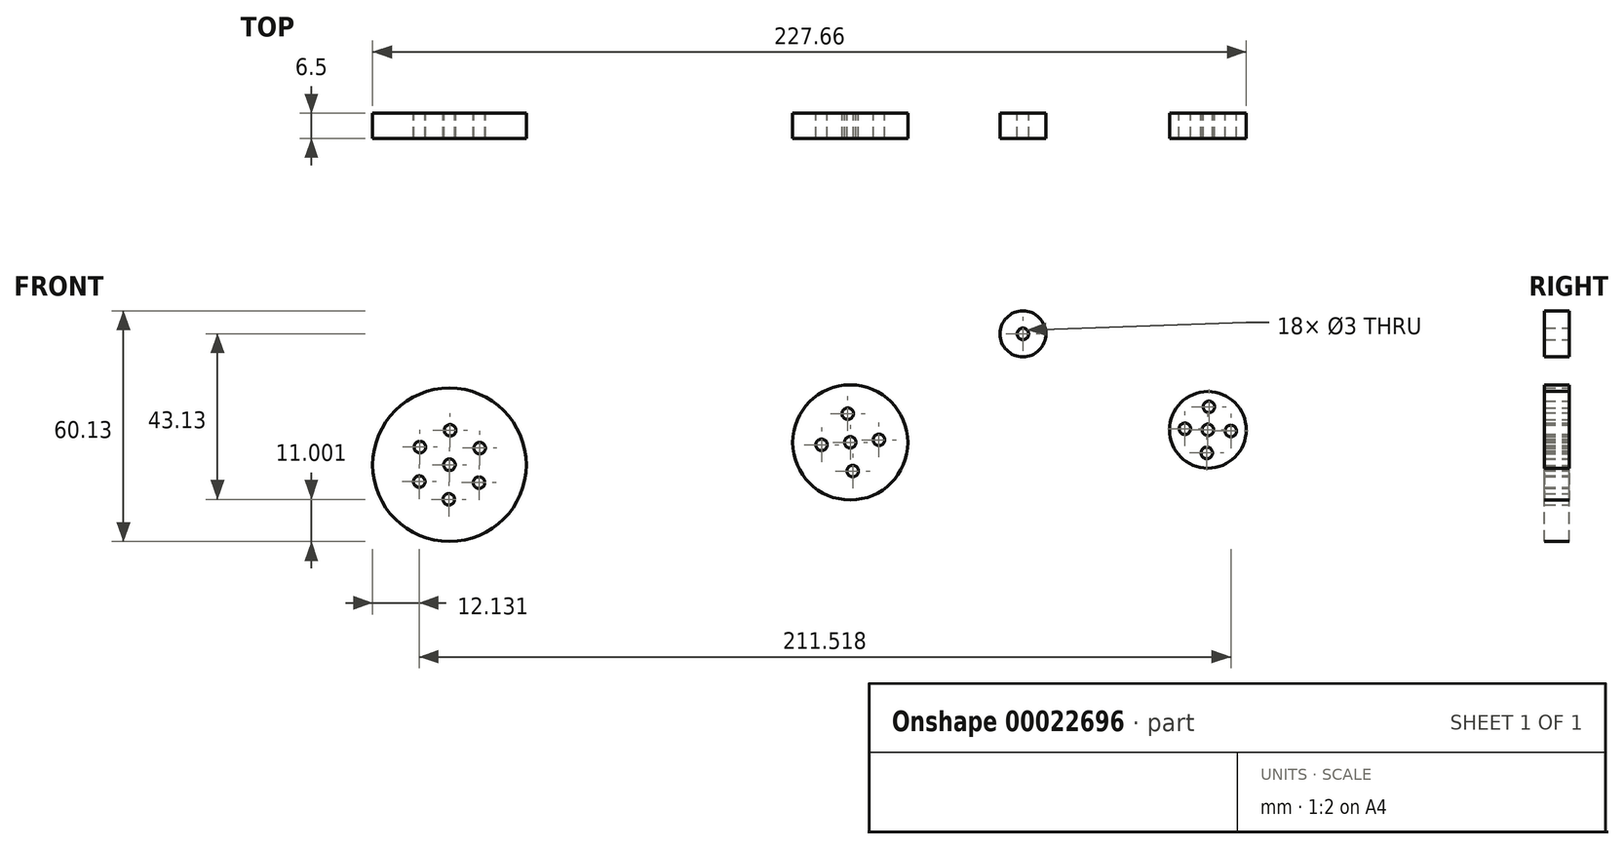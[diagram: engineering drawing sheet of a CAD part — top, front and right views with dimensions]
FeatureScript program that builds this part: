
annotation { "Feature Type Name" : "Feature", "Feature Type Description" : "" }
export const myFeature = defineFeature(function(context is Context, id is Id, definition is map)
    precondition{}
    {
        {
            var Q0;
            Q0=qCreatedBy(makeId("Front.planeOp"),FACE);
            var sketch = newSketch(context, id + "F0", { "sketchPlane" : qUnion([Q0])});
            skCircle(sketch, "E0", {"center": v(-166.59, 0) * mm, "radius": 20 * mm});
            skPoint(sketch, "E1", {"position": v(-166.59, -20) * mm});
            skCircle(sketch, "E2", {"center": v(-166.59, 0) * mm, "radius": 1.5 * mm});
            skPoint(sketch, "E3", {"position": v(-166.62, 1.5) * mm});
            skCircle(sketch, "E4", {"center": v(-166.59, 0) * mm, "radius": 18 * mm});
            skCircle(sketch, "E5", {"center": v(-166.59, 0) * mm, "radius": 3.5 * mm});
            skCircle(sketch, "E6", {"center": v(-158.87, -4.64) * mm, "radius": 1.5 * mm});
            skLineSegment(sketch, "E7", {"start": v(-166.59, 0) * mm, "end": v(-158.87, -4.64) * mm});
            skCircle(sketch, "E8.1.0", {"center": v(-158.71, 4.36) * mm, "radius": 1.5 * mm});
            skCircle(sketch, "E8.2.0", {"center": v(-166.43, 9) * mm, "radius": 1.5 * mm});
            skCircle(sketch, "E8.3.0", {"center": v(-174.3, 4.64) * mm, "radius": 1.5 * mm});
            skCircle(sketch, "E8.4.0", {"center": v(-174.46, -4.36) * mm, "radius": 1.5 * mm});
            skCircle(sketch, "E8.5.0", {"center": v(-166.75, -9) * mm, "radius": 1.5 * mm});
            skSolve(sketch);
        }
        {
            var Q0;
            Q0=makeQuery(id+"F0.imprint","IMPRINT",FACE,{"disambiguationData":[TD([[makeQuery(id+"F0.imprint","IMPRINT",EDGE,{"derivedFrom":sQuery(id+"F0.wireOp",EDGE,"E4")}),1.0]])]});
            var Q1;
            Q1=makeQuery(id+"F0.imprint","IMPRINT",FACE,{"disambiguationData":[TD([[makeQuery(id+"F0.imprint","IMPRINT",EDGE,{"derivedFrom":sQuery(id+"F0.wireOp",EDGE,"E0")}),1.0]])]});
            var Q2;
            Q2=makeQuery(id+"F0.imprint","IMPRINT",FACE,{"disambiguationData":[TD([[makeQuery(id+"F0.imprint","IMPRINT",EDGE,{"derivedFrom":sQuery(id+"F0.wireOp",EDGE,"E2")}),-1.0]])]});
            extrude(context, id + "F1", {"entities" : qUnion([Q0, Q1, Q2]), "depth" : 6.5 * mm});
        }
        {
            var Q0;
            Q0=qCreatedBy(makeId("Front.planeOp"),FACE);
            var sketch = newSketch(context, id + "F2", { "sketchPlane" : qUnion([Q0])});
            skCircle(sketch, "E9", {"center": v(-62.13, 5.85) * mm, "radius": 15 * mm});
            skCircle(sketch, "E10", {"center": v(-62.13, 5.85) * mm, "radius": 3.5 * mm});
            skCircle(sketch, "E11", {"center": v(-62.13, 5.85) * mm, "radius": 1.5 * mm});
            skCircle(sketch, "E12", {"center": v(-62.78, 13.32) * mm, "radius": 1.5 * mm});
            skLineSegment(sketch, "E13", {"start": v(-62.13, 5.85) * mm, "end": v(-62.78, 13.32) * mm});
            skCircle(sketch, "E14", {"center": v(-62.13, 5.85) * mm, "radius": 12 * mm});
            skCircle(sketch, "E15.1.0", {"center": v(-69.6, 5.2) * mm, "radius": 1.5 * mm});
            skCircle(sketch, "E15.2.0", {"center": v(-61.48, -1.62) * mm, "radius": 1.5 * mm});
            skCircle(sketch, "E16.1.3.0", {"center": v(-54.66, 6.5) * mm, "radius": 1.5 * mm});
            skSolve(sketch);
        }
        {
            var Q0;
            Q0=makeQuery(id+"F2.imprint","IMPRINT",FACE,{"disambiguationData":[TD([[makeQuery(id+"F2.imprint","IMPRINT",EDGE,{"derivedFrom":sQuery(id+"F2.wireOp",EDGE,"E10")}),-1.0]])]});
            var Q1;
            Q1=makeQuery(id+"F2.imprint","IMPRINT",FACE,{"disambiguationData":[TD([[makeQuery(id+"F2.imprint","IMPRINT",EDGE,{"derivedFrom":sQuery(id+"F2.wireOp",EDGE,"E9")}),1.0]])]});
            var Q2;
            Q2=makeQuery(id+"F2.imprint","IMPRINT",FACE,{"disambiguationData":[TD([[makeQuery(id+"F2.imprint","IMPRINT",EDGE,{"derivedFrom":sQuery(id+"F2.wireOp",EDGE,"E10")}),1.0]])]});
            extrude(context, id + "F3", {"entities" : qUnion([Q0, Q1, Q2]), "depth" : 6.5 * mm});
        }
        {
            var Q0;
            Q0=qCreatedBy(makeId("Front.planeOp"),FACE);
            var sketch = newSketch(context, id + "F4", { "sketchPlane" : qUnion([Q0])});
            skCircle(sketch, "E17", {"center": v(31.07, 9.1) * mm, "radius": 10 * mm});
            skCircle(sketch, "E18", {"center": v(31.07, 9.1) * mm, "radius": 1.5 * mm});
            skCircle(sketch, "E19", {"center": v(31.07, 9.1) * mm, "radius": 3.5 * mm});
            skCircle(sketch, "E20", {"center": v(31.35, 15.1) * mm, "radius": 1.5 * mm});
            skLineSegment(sketch, "E21", {"start": v(31.07, 9.1) * mm, "end": v(31.35, 15.1) * mm});
            skCircle(sketch, "E22.1.0", {"center": v(25.07, 9.4) * mm, "radius": 1.5 * mm});
            skCircle(sketch, "E22.2.0", {"center": v(30.78, 3.12) * mm, "radius": 1.5 * mm});
            skCircle(sketch, "E22.3.0", {"center": v(37.06, 8.83) * mm, "radius": 1.5 * mm});
            skCircle(sketch, "E23", {"center": v(31.07, 9.1) * mm, "radius": 8.5 * mm});
            skSolve(sketch);
        }
        {
            var Q0;
            Q0=makeQuery(id+"F4.imprint","IMPRINT",FACE,{"disambiguationData":[TD([[makeQuery(id+"F4.imprint","IMPRINT",EDGE,{"derivedFrom":sQuery(id+"F4.wireOp",EDGE,"E19")}),-1.0]])]});
            var Q1;
            Q1=makeQuery(id+"F4.imprint","IMPRINT",FACE,{"disambiguationData":[TD([[makeQuery(id+"F4.imprint","IMPRINT",EDGE,{"derivedFrom":sQuery(id+"F4.wireOp",EDGE,"E18")}),-1.0]])]});
            var Q2;
            Q2=makeQuery(id+"F4.imprint","IMPRINT",FACE,{"disambiguationData":[TD([[makeQuery(id+"F4.imprint","IMPRINT",EDGE,{"derivedFrom":sQuery(id+"F4.wireOp",EDGE,"E17")}),1.0]])]});
            extrude(context, id + "F5", {"entities" : qUnion([Q0, Q1, Q2]), "depth" : 6.5 * mm});
        }
        {
            var Q0;
            Q0=qCreatedBy(makeId("Front.planeOp"),FACE);
            var sketch = newSketch(context, id + "F6", { "sketchPlane" : qUnion([Q0])});
            skCircle(sketch, "E24", {"center": v(-17.12, 34.13) * mm, "radius": 6 * mm});
            skCircle(sketch, "E25", {"center": v(-17.12, 34.13) * mm, "radius": 4.5 * mm});
            skCircle(sketch, "E26", {"center": v(-17.12, 34.13) * mm, "radius": 1.5 * mm});
            skSolve(sketch);
        }
        {
            var Q0;
            Q0=makeQuery(id+"F6.imprint","IMPRINT",FACE,{"disambiguationData":[TD([[makeQuery(id+"F6.imprint","IMPRINT",EDGE,{"derivedFrom":sQuery(id+"F6.wireOp",EDGE,"E25")}),1.0]])]});
            var Q1;
            Q1=makeQuery(id+"F6.imprint","IMPRINT",FACE,{"disambiguationData":[TD([[makeQuery(id+"F6.imprint","IMPRINT",EDGE,{"derivedFrom":sQuery(id+"F6.wireOp",EDGE,"E24")}),1.0]])]});
            extrude(context, id + "F7", {"entities" : qUnion([Q0, Q1]), "depth" : 6.5 * mm});
        }
    });
